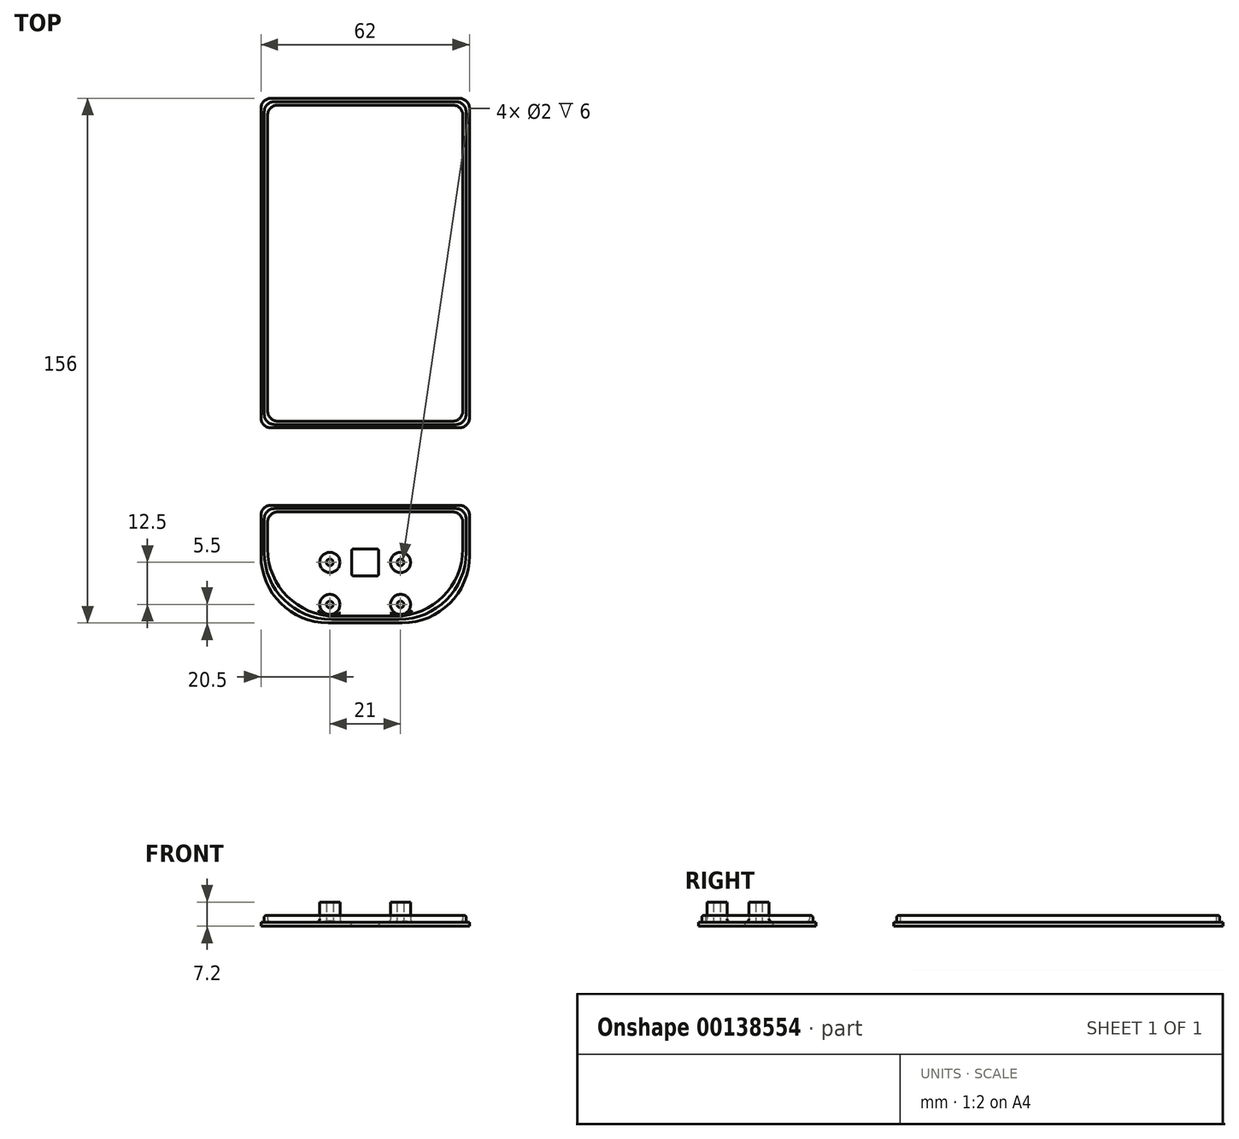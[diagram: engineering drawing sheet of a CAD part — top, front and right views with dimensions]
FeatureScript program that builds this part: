
annotation { "Feature Type Name" : "Feature", "Feature Type Description" : "" }
export const myFeature = defineFeature(function(context is Context, id is Id, definition is map)
    precondition{}
    {
        {
            var Q0;
            Q0=qCreatedBy(makeId("Top.planeOp"),FACE);
            var sketch = newSketch(context, id + "F0", { "sketchPlane" : qUnion([Q0])});
            skLineSegment(sketch, "E0.bottom", {"start": v(-27, 48) * mm, "end": v(27, 48) * mm});
            skLineSegment(sketch, "E0.top", {"start": v(-27, -48) * mm, "end": v(27, -48) * mm});
            skLineSegment(sketch, "E0.left", {"start": v(-30, 45) * mm, "end": v(-30, -45) * mm});
            skLineSegment(sketch, "E0.right", {"start": v(30, 45) * mm, "end": v(30, -45) * mm});
            skPoint(sketch, "E0.middle", {"position": v(0, 0) * mm});
            skPoint(sketch, "E1.visualSharp", {"position": v(-30, 48) * mm});
            skArc(sketch, "E1.filletArc", {"start": v(-27, 48) * mm, "mid": v(-29.12, 47.12) * mm, "end": v(-30, 45) * mm});
            skPoint(sketch, "E2.visualSharp", {"position": v(30, 48) * mm});
            skArc(sketch, "E2.filletArc", {"start": v(30, 45) * mm, "mid": v(29.12, 47.12) * mm, "end": v(27, 48) * mm});
            skPoint(sketch, "E3.visualSharp", {"position": v(30, -48) * mm});
            skArc(sketch, "E3.filletArc", {"start": v(27, -48) * mm, "mid": v(29.12, -47.12) * mm, "end": v(30, -45) * mm});
            skPoint(sketch, "E4.visualSharp", {"position": v(-30, -48) * mm});
            skArc(sketch, "E4.filletArc", {"start": v(-30, -45) * mm, "mid": v(-29.12, -47.12) * mm, "end": v(-27, -48) * mm});
            skLineSegment(sketch, "E5.bottom", {"start": v(-28, 49) * mm, "end": v(28, 49) * mm});
            skLineSegment(sketch, "E5.top", {"start": v(-28, -49) * mm, "end": v(28, -49) * mm});
            skLineSegment(sketch, "E5.left", {"start": v(-31, 46) * mm, "end": v(-31, -46) * mm});
            skLineSegment(sketch, "E5.right", {"start": v(31, 46) * mm, "end": v(31, -46) * mm});
            skPoint(sketch, "E6.visualSharp", {"position": v(-31, -49) * mm});
            skArc(sketch, "E6.filletArc", {"start": v(-31, -46) * mm, "mid": v(-30.12, -48.12) * mm, "end": v(-28, -49) * mm});
            skPoint(sketch, "E7.visualSharp", {"position": v(31, -49) * mm});
            skArc(sketch, "E7.filletArc", {"start": v(28, -49) * mm, "mid": v(30.12, -48.12) * mm, "end": v(31, -46) * mm});
            skPoint(sketch, "E8.visualSharp", {"position": v(31, 49) * mm});
            skArc(sketch, "E8.filletArc", {"start": v(31, 46) * mm, "mid": v(30.12, 48.12) * mm, "end": v(28, 49) * mm});
            skPoint(sketch, "E9.visualSharp", {"position": v(-31, 49) * mm});
            skArc(sketch, "E9.filletArc", {"start": v(-28, 49) * mm, "mid": v(-30.12, 48.12) * mm, "end": v(-31, 46) * mm});
            skLineSegment(sketch, "E10", {"start": v(0, 0) * mm, "end": v(0, 68.08) * mm, "construction": true});
            skPoint(sketch, "E10.endSnap0", {"position": v(0, 48) * mm});
            skPoint(sketch, "E11", {"position": v(0, 42) * mm});
            skLineSegment(sketch, "E12", {"start": v(0, 0) * mm, "end": v(0, -48) * mm, "construction": true});
            skLineSegment(sketch, "E13.bottom", {"start": v(-28, -72) * mm, "end": v(28, -72) * mm});
            skLineSegment(sketch, "E13.top", {"start": v(-11, -107) * mm, "end": v(11, -107) * mm});
            skLineSegment(sketch, "E13.left", {"start": v(-31, -75) * mm, "end": v(-31, -87) * mm});
            skLineSegment(sketch, "E13.right", {"start": v(31, -75) * mm, "end": v(31, -87) * mm});
            skLineSegment(sketch, "E14", {"start": v(0, 1.02) * mm, "end": v(0, 0) * mm, "construction": true});
            skPoint(sketch, "E14.endSnap0", {"position": v(0, -24) * mm});
            skPoint(sketch, "E15", {"position": v(0, -72) * mm});
            skLineSegment(sketch, "E16", {"start": v(-31, -42.86) * mm, "end": v(-31, -72) * mm, "construction": true});
            skLineSegment(sketch, "E17.bottom", {"start": v(-10, -106) * mm, "end": v(10, -106) * mm});
            skLineSegment(sketch, "E17.top", {"start": v(-27, -73) * mm, "end": v(27, -73) * mm});
            skLineSegment(sketch, "E17.left", {"start": v(-30, -86) * mm, "end": v(-30, -76) * mm});
            skLineSegment(sketch, "E17.right", {"start": v(30, -86) * mm, "end": v(30, -76) * mm});
            skPoint(sketch, "E18.visualSharp", {"position": v(-30, -106) * mm});
            skArc(sketch, "E18.filletArc", {"start": v(-30, -86) * mm, "mid": v(-24.14, -100.14) * mm, "end": v(-10, -106) * mm});
            skPoint(sketch, "E19.visualSharp", {"position": v(-30, -73) * mm});
            skArc(sketch, "E19.filletArc", {"start": v(-27, -73) * mm, "mid": v(-29.12, -73.88) * mm, "end": v(-30, -76) * mm});
            skPoint(sketch, "E20.visualSharp", {"position": v(30, -73) * mm});
            skArc(sketch, "E20.filletArc", {"start": v(30, -76) * mm, "mid": v(29.12, -73.88) * mm, "end": v(27, -73) * mm});
            skPoint(sketch, "E21.visualSharp", {"position": v(30, -106) * mm});
            skArc(sketch, "E21.filletArc", {"start": v(10, -106) * mm, "mid": v(24.14, -100.14) * mm, "end": v(30, -86) * mm});
            skPoint(sketch, "E22.visualSharp", {"position": v(-31, -72) * mm});
            skArc(sketch, "E22.filletArc", {"start": v(-28, -72) * mm, "mid": v(-30.12, -72.88) * mm, "end": v(-31, -75) * mm});
            skPoint(sketch, "E23.visualSharp", {"position": v(31, -72) * mm});
            skArc(sketch, "E23.filletArc", {"start": v(31, -75) * mm, "mid": v(30.12, -72.88) * mm, "end": v(28, -72) * mm});
            skPoint(sketch, "E24.visualSharp", {"position": v(-31, -107) * mm});
            skArc(sketch, "E24.filletArc", {"start": v(-31, -87) * mm, "mid": v(-25.14, -101.14) * mm, "end": v(-11, -107) * mm});
            skPoint(sketch, "E25.visualSharp", {"position": v(31, -107) * mm});
            skArc(sketch, "E25.filletArc", {"start": v(11, -107) * mm, "mid": v(25.14, -101.14) * mm, "end": v(31, -87) * mm});
            skLineSegment(sketch, "E26.bottom", {"start": v(-26, 47) * mm, "end": v(26, 47) * mm});
            skLineSegment(sketch, "E26.top", {"start": v(-26, -47) * mm, "end": v(26, -47) * mm});
            skLineSegment(sketch, "E26.left", {"start": v(-29, 44) * mm, "end": v(-29, -44) * mm});
            skLineSegment(sketch, "E26.right", {"start": v(29, 44) * mm, "end": v(29, -44) * mm});
            skPoint(sketch, "E27.visualSharp", {"position": v(-29, 47) * mm});
            skArc(sketch, "E27.filletArc", {"start": v(-26, 47) * mm, "mid": v(-28.12, 46.12) * mm, "end": v(-29, 44) * mm});
            skPoint(sketch, "E28.visualSharp", {"position": v(29, 47) * mm});
            skArc(sketch, "E28.filletArc", {"start": v(29, 44) * mm, "mid": v(28.12, 46.12) * mm, "end": v(26, 47) * mm});
            skPoint(sketch, "E29.visualSharp", {"position": v(29, -47) * mm});
            skArc(sketch, "E29.filletArc", {"start": v(26, -47) * mm, "mid": v(28.12, -46.12) * mm, "end": v(29, -44) * mm});
            skPoint(sketch, "E30.visualSharp", {"position": v(-29, -47) * mm});
            skArc(sketch, "E30.filletArc", {"start": v(-29, -44) * mm, "mid": v(-28.12, -46.12) * mm, "end": v(-26, -47) * mm});
            skLineSegment(sketch, "E31.bottom", {"start": v(-26, -74) * mm, "end": v(26, -74) * mm});
            skLineSegment(sketch, "E31.top", {"start": v(-9, -105) * mm, "end": v(9, -105) * mm});
            skLineSegment(sketch, "E31.left", {"start": v(-29, -77) * mm, "end": v(-29, -85) * mm});
            skLineSegment(sketch, "E31.right", {"start": v(29, -77) * mm, "end": v(29, -85) * mm});
            skPoint(sketch, "E31.middle", {"position": v(0, -89.5) * mm});
            skPoint(sketch, "E32.visualSharp", {"position": v(-29, -74) * mm});
            skArc(sketch, "E32.filletArc", {"start": v(-26, -74) * mm, "mid": v(-28.12, -74.88) * mm, "end": v(-29, -77) * mm});
            skPoint(sketch, "E33.visualSharp", {"position": v(29, -74) * mm});
            skArc(sketch, "E33.filletArc", {"start": v(29, -77) * mm, "mid": v(28.12, -74.88) * mm, "end": v(26, -74) * mm});
            skPoint(sketch, "E34.visualSharp", {"position": v(-29, -105) * mm});
            skArc(sketch, "E34.filletArc", {"start": v(-29, -85) * mm, "mid": v(-23.14, -99.14) * mm, "end": v(-9, -105) * mm});
            skPoint(sketch, "E35.visualSharp", {"position": v(29, -105) * mm});
            skArc(sketch, "E35.filletArc", {"start": v(9, -105) * mm, "mid": v(23.14, -99.14) * mm, "end": v(29, -85) * mm});
            skLineSegment(sketch, "E36", {"start": v(0, 1.02) * mm, "end": v(0, -119.3) * mm, "construction": true});
            skPoint(sketch, "E36.endSnap0", {"position": v(0, -105) * mm});
            skLineSegment(sketch, "E37.bottom", {"start": v(10.5, -101.5) * mm, "end": v(-10.5, -101.5) * mm});
            skLineSegment(sketch, "E37.top", {"start": v(10.5, -89) * mm, "end": v(-10.5, -89) * mm});
            skLineSegment(sketch, "E37.left", {"start": v(10.5, -101.5) * mm, "end": v(10.5, -89) * mm});
            skLineSegment(sketch, "E37.right", {"start": v(-10.5, -101.5) * mm, "end": v(-10.5, -89) * mm});
            skPoint(sketch, "E37.middle", {"position": v(0, -95.25) * mm});
            skCircle(sketch, "E38", {"center": v(10.5, -101.5) * mm, "radius": 1 * mm});
            skCircle(sketch, "E39", {"center": v(-10.5, -101.5) * mm, "radius": 1 * mm});
            skCircle(sketch, "E40", {"center": v(-10.5, -89) * mm, "radius": 1 * mm});
            skCircle(sketch, "E41", {"center": v(10.5, -89) * mm, "radius": 1 * mm});
            skCircle(sketch, "E42", {"center": v(10.5, -101.5) * mm, "radius": 3 * mm});
            skCircle(sketch, "E43", {"center": v(10.5, -89) * mm, "radius": 3 * mm});
            skCircle(sketch, "E44", {"center": v(-10.5, -101.5) * mm, "radius": 3 * mm});
            skCircle(sketch, "E45", {"center": v(-10.5, -89) * mm, "radius": 3 * mm});
            skLineSegment(sketch, "E46.bottom", {"start": v(4, -93) * mm, "end": v(-4, -93) * mm});
            skLineSegment(sketch, "E46.top", {"start": v(4, -85) * mm, "end": v(-4, -85) * mm});
            skLineSegment(sketch, "E46.left", {"start": v(4, -93) * mm, "end": v(4, -85) * mm});
            skLineSegment(sketch, "E46.right", {"start": v(-4, -93) * mm, "end": v(-4, -85) * mm});
            skSolve(sketch);
        }
        {
            var Q0;
            Q0=makeQuery(id+"F0.imprint","IMPRINT",FACE,{"disambiguationData":[TD([[makeQuery(id+"F0.imprint","IMPRINT",EDGE,{"derivedFrom":sQuery(id+"F0.wireOp",EDGE,"E0.bottom")}),1.0]])]});
            var Q1;
            Q1=makeQuery(id+"F0.imprint","IMPRINT",FACE,{"disambiguationData":[TD([[makeQuery(id+"F0.imprint","IMPRINT",EDGE,{"derivedFrom":sQuery(id+"F0.wireOp",EDGE,"E0.bottom")}),-1.0]])]});
            var Q2;
            Q2=makeQuery(id+"F0.imprint","IMPRINT",FACE,{"disambiguationData":[TD([[makeQuery(id+"F0.imprint","IMPRINT",EDGE,{"derivedFrom":sQuery(id+"F0.wireOp",EDGE,"E17.bottom")}),1.0]])]});
            var Q3;
            Q3=makeQuery(id+"F0.imprint","IMPRINT",FACE,{"disambiguationData":[TD([[makeQuery(id+"F0.imprint","IMPRINT",EDGE,{"derivedFrom":sQuery(id+"F0.wireOp",EDGE,"E13.bottom")}),-1.0]])]});
            var Q4;
            Q4=makeQuery(id+"F0.imprint","IMPRINT",FACE,{"disambiguationData":[TD([[makeQuery(id+"F0.imprint","IMPRINT",EDGE,{"derivedFrom":sQuery(id+"F0.wireOp",EDGE,"E26.bottom")}),-1.0]])]});
            var Q5;
            Q5=makeQuery(id+"F0.imprint","IMPRINT",FACE,{"disambiguationData":[TD([[makeQuery(id+"F0.imprint","IMPRINT",EDGE,{"derivedFrom":sQuery(id+"F0.wireOp",EDGE,"E31.bottom")}),-1.0]])]});
            var Q6;
            {var subQ0=sQuery(id+"F0.wireOp",EDGE,"E42");var subQ13=sQuery(id+"F0.wireOp",EDGE,"E37.bottom");var subQ14=makeQuery(id+"F0.imprint","INTERSECT",VERTEX,{"derivedFrom":[subQ13,subQ0]});Q6=makeQuery(id+"F0.imprint","IMPRINT",FACE,{"disambiguationData":[TD([[makeQuery(id+"F0.imprint","IMPRINT",EDGE,{"disambiguationData":[TD([[subQ14,-1.0]])],"derivedFrom":subQ13}),-1.0]])]});}
            var Q7;
            {var subQ0=sQuery(id+"F0.wireOp",EDGE,"E44");var subQ1=sQuery(id+"F0.wireOp",EDGE,"E37.bottom");var subQ2=makeQuery(id+"F0.imprint","INTERSECT",VERTEX,{"derivedFrom":[subQ1,subQ0]});Q7=makeQuery(id+"F0.imprint","IMPRINT",FACE,{"disambiguationData":[TD([[makeQuery(id+"F0.imprint","IMPRINT",EDGE,{"disambiguationData":[TD([[subQ2,-1.0]])],"derivedFrom":subQ1}),1.0]])]});}
            var Q8;
            {var subQ0=sQuery(id+"F0.wireOp",EDGE,"E44");var subQ1=sQuery(id+"F0.wireOp",EDGE,"E37.bottom");var subQ2=makeQuery(id+"F0.imprint","INTERSECT",VERTEX,{"derivedFrom":[subQ1,subQ0]});Q8=makeQuery(id+"F0.imprint","IMPRINT",FACE,{"disambiguationData":[TD([[makeQuery(id+"F0.imprint","IMPRINT",EDGE,{"disambiguationData":[TD([[subQ2,-1.0]])],"derivedFrom":subQ1}),-1.0]])]});}
            var Q9;
            {var subQ0=sQuery(id+"F0.wireOp",EDGE,"E45");var subQ1=sQuery(id+"F0.wireOp",EDGE,"E37.top");var subQ2=makeQuery(id+"F0.imprint","INTERSECT",VERTEX,{"derivedFrom":[subQ1,subQ0]});Q9=makeQuery(id+"F0.imprint","IMPRINT",FACE,{"disambiguationData":[TD([[makeQuery(id+"F0.imprint","IMPRINT",EDGE,{"disambiguationData":[TD([[subQ2,-1.0]])],"derivedFrom":subQ1}),-1.0]])]});}
            var Q10;
            {var subQ0=sQuery(id+"F0.wireOp",EDGE,"E45");var subQ1=sQuery(id+"F0.wireOp",EDGE,"E37.top");var subQ2=makeQuery(id+"F0.imprint","INTERSECT",VERTEX,{"derivedFrom":[subQ1,subQ0]});Q10=makeQuery(id+"F0.imprint","IMPRINT",FACE,{"disambiguationData":[TD([[makeQuery(id+"F0.imprint","IMPRINT",EDGE,{"disambiguationData":[TD([[subQ2,-1.0]])],"derivedFrom":subQ1}),1.0]])]});}
            var Q11;
            {var subQ0=sQuery(id+"F0.wireOp",EDGE,"E37.right");var subQ1=sQuery(id+"F0.wireOp",EDGE,"E37.top");var subQ2=makeQuery(id+"F0.imprint","INTERSECT",VERTEX,{"derivedFrom":[subQ1,subQ0]});Q11=makeQuery(id+"F0.imprint","IMPRINT",FACE,{"disambiguationData":[TD([[makeQuery(id+"F0.imprint","IMPRINT",EDGE,{"disambiguationData":[TD([[subQ2,1.0]])],"derivedFrom":subQ1}),-1.0]])]});}
            var Q12;
            {var subQ0=sQuery(id+"F0.wireOp",EDGE,"E37.right");var subQ1=sQuery(id+"F0.wireOp",EDGE,"E37.bottom");var subQ2=makeQuery(id+"F0.imprint","INTERSECT",VERTEX,{"derivedFrom":[subQ1,subQ0]});Q12=makeQuery(id+"F0.imprint","IMPRINT",FACE,{"disambiguationData":[TD([[makeQuery(id+"F0.imprint","IMPRINT",EDGE,{"disambiguationData":[TD([[subQ2,1.0]])],"derivedFrom":subQ1}),1.0]])]});}
            var Q13;
            {var subQ0=sQuery(id+"F0.wireOp",EDGE,"E37.right");var subQ1=sQuery(id+"F0.wireOp",EDGE,"E37.bottom");var subQ2=makeQuery(id+"F0.imprint","INTERSECT",VERTEX,{"derivedFrom":[subQ1,subQ0]});Q13=makeQuery(id+"F0.imprint","IMPRINT",FACE,{"disambiguationData":[TD([[makeQuery(id+"F0.imprint","IMPRINT",EDGE,{"disambiguationData":[TD([[subQ2,1.0]])],"derivedFrom":subQ1}),-1.0]])]});}
            var Q14;
            {var subQ0=sQuery(id+"F0.wireOp",EDGE,"E37.right");var subQ1=sQuery(id+"F0.wireOp",EDGE,"E37.top");var subQ2=makeQuery(id+"F0.imprint","INTERSECT",VERTEX,{"derivedFrom":[subQ1,subQ0]});Q14=makeQuery(id+"F0.imprint","IMPRINT",FACE,{"disambiguationData":[TD([[makeQuery(id+"F0.imprint","IMPRINT",EDGE,{"disambiguationData":[TD([[subQ2,1.0]])],"derivedFrom":subQ1}),1.0]])]});}
            var Q15;
            {var subQ0=sQuery(id+"F0.wireOp",EDGE,"E41");var subQ1=sQuery(id+"F0.wireOp",EDGE,"E37.top");var subQ2=makeQuery(id+"F0.imprint","INTERSECT",VERTEX,{"derivedFrom":[subQ1,subQ0]});Q15=makeQuery(id+"F0.imprint","IMPRINT",FACE,{"disambiguationData":[TD([[makeQuery(id+"F0.imprint","IMPRINT",EDGE,{"disambiguationData":[TD([[subQ2,-1.0]])],"derivedFrom":subQ1}),1.0]])]});}
            var Q16;
            {var subQ0=sQuery(id+"F0.wireOp",EDGE,"E41");var subQ1=sQuery(id+"F0.wireOp",EDGE,"E37.top");var subQ2=makeQuery(id+"F0.imprint","INTERSECT",VERTEX,{"derivedFrom":[subQ1,subQ0]});Q16=makeQuery(id+"F0.imprint","IMPRINT",FACE,{"disambiguationData":[TD([[makeQuery(id+"F0.imprint","IMPRINT",EDGE,{"disambiguationData":[TD([[subQ2,-1.0]])],"derivedFrom":subQ1}),-1.0]])]});}
            var Q17;
            {var subQ0=sQuery(id+"F0.wireOp",EDGE,"E37.left");var subQ1=sQuery(id+"F0.wireOp",EDGE,"E37.top");var subQ2=makeQuery(id+"F0.imprint","INTERSECT",VERTEX,{"derivedFrom":[subQ1,subQ0]});Q17=makeQuery(id+"F0.imprint","IMPRINT",FACE,{"disambiguationData":[TD([[makeQuery(id+"F0.imprint","IMPRINT",EDGE,{"disambiguationData":[TD([[subQ2,-1.0]])],"derivedFrom":subQ1}),-1.0]])]});}
            var Q18;
            {var subQ0=sQuery(id+"F0.wireOp",EDGE,"E37.left");var subQ1=sQuery(id+"F0.wireOp",EDGE,"E37.top");var subQ2=makeQuery(id+"F0.imprint","INTERSECT",VERTEX,{"derivedFrom":[subQ1,subQ0]});Q18=makeQuery(id+"F0.imprint","IMPRINT",FACE,{"disambiguationData":[TD([[makeQuery(id+"F0.imprint","IMPRINT",EDGE,{"disambiguationData":[TD([[subQ2,-1.0]])],"derivedFrom":subQ1}),1.0]])]});}
            var Q19;
            {var subQ0=sQuery(id+"F0.wireOp",EDGE,"E38");var subQ1=sQuery(id+"F0.wireOp",EDGE,"E37.bottom");var subQ2=makeQuery(id+"F0.imprint","INTERSECT",VERTEX,{"derivedFrom":[subQ1,subQ0]});Q19=makeQuery(id+"F0.imprint","IMPRINT",FACE,{"disambiguationData":[TD([[makeQuery(id+"F0.imprint","IMPRINT",EDGE,{"disambiguationData":[TD([[subQ2,-1.0]])],"derivedFrom":subQ1}),-1.0]])]});}
            var Q20;
            {var subQ0=sQuery(id+"F0.wireOp",EDGE,"E38");var subQ1=sQuery(id+"F0.wireOp",EDGE,"E37.bottom");var subQ2=makeQuery(id+"F0.imprint","INTERSECT",VERTEX,{"derivedFrom":[subQ1,subQ0]});Q20=makeQuery(id+"F0.imprint","IMPRINT",FACE,{"disambiguationData":[TD([[makeQuery(id+"F0.imprint","IMPRINT",EDGE,{"disambiguationData":[TD([[subQ2,-1.0]])],"derivedFrom":subQ1}),1.0]])]});}
            var Q21;
            {var subQ0=sQuery(id+"F0.wireOp",EDGE,"E37.left");var subQ1=sQuery(id+"F0.wireOp",EDGE,"E37.bottom");var subQ2=makeQuery(id+"F0.imprint","INTERSECT",VERTEX,{"derivedFrom":[subQ1,subQ0]});Q21=makeQuery(id+"F0.imprint","IMPRINT",FACE,{"disambiguationData":[TD([[makeQuery(id+"F0.imprint","IMPRINT",EDGE,{"disambiguationData":[TD([[subQ2,-1.0]])],"derivedFrom":subQ1}),1.0]])]});}
            var Q22;
            {var subQ0=sQuery(id+"F0.wireOp",EDGE,"E37.left");var subQ1=sQuery(id+"F0.wireOp",EDGE,"E37.bottom");var subQ2=makeQuery(id+"F0.imprint","INTERSECT",VERTEX,{"derivedFrom":[subQ1,subQ0]});Q22=makeQuery(id+"F0.imprint","IMPRINT",FACE,{"disambiguationData":[TD([[makeQuery(id+"F0.imprint","IMPRINT",EDGE,{"disambiguationData":[TD([[subQ2,-1.0]])],"derivedFrom":subQ1}),-1.0]])]});}
            extrude(context, id + "F1", {"entities" : qUnion([Q0, Q1, Q2, Q3, Q4, Q5, Q6, Q7, Q8, Q9, Q10, Q11, Q12, Q13, Q14, Q15, Q16, Q17, Q18, Q19, Q20, Q21, Q22]), "oppositeDirection" : true, "depth" : 1.2 * mm});
        }
        {
            var Q0;
            Q0=makeQuery(id+"F0.imprint","IMPRINT",FACE,{"disambiguationData":[TD([[makeQuery(id+"F0.imprint","IMPRINT",EDGE,{"derivedFrom":sQuery(id+"F0.wireOp",EDGE,"E17.bottom")}),1.0]])]});
            var Q1;
            Q1=makeQuery(id+"F0.imprint","IMPRINT",FACE,{"disambiguationData":[TD([[makeQuery(id+"F0.imprint","IMPRINT",EDGE,{"derivedFrom":sQuery(id+"F0.wireOp",EDGE,"E0.bottom")}),-1.0]])]});
            extrude(context, id + "F2", {"entities" : qUnion([Q0, Q1]), "operationType" : NewBodyOperationType.ADD, "depth" : 2 * mm});
        }
        {
            var Q0;
            Q0=makeQuery(id+"F2.opExtrude","CAP_EDGE",EDGE,{"disambiguationData":[OSD([sQuery(id+"F0.wireOp",EDGE,"E0.left")])],"isStart":false});
            var Q1;
            Q1=makeQuery(id+"F2.opExtrude","CAP_EDGE",EDGE,{"disambiguationData":[OSD([sQuery(id+"F0.wireOp",EDGE,"E0.bottom")])],"isStart":false});
            var Q2;
            Q2=makeQuery(id+"F2.opExtrude","CAP_EDGE",EDGE,{"disambiguationData":[OSD([sQuery(id+"F0.wireOp",EDGE,"E1.filletArc")])],"isStart":false});
            var Q3;
            Q3=makeQuery(id+"F2.opExtrude","CAP_EDGE",EDGE,{"disambiguationData":[OSD([sQuery(id+"F0.wireOp",EDGE,"E2.filletArc")])],"isStart":false});
            var Q4;
            Q4=makeQuery(id+"F2.opExtrude","CAP_EDGE",EDGE,{"disambiguationData":[OSD([sQuery(id+"F0.wireOp",EDGE,"E0.right")])],"isStart":false});
            var Q5;
            Q5=makeQuery(id+"F2.opExtrude","CAP_EDGE",EDGE,{"disambiguationData":[OSD([sQuery(id+"F0.wireOp",EDGE,"E4.filletArc")])],"isStart":false});
            var Q6;
            Q6=makeQuery(id+"F2.opExtrude","CAP_EDGE",EDGE,{"disambiguationData":[OSD([sQuery(id+"F0.wireOp",EDGE,"E0.top")])],"isStart":false});
            var Q7;
            Q7=makeQuery(id+"F2.opExtrude","CAP_EDGE",EDGE,{"disambiguationData":[OSD([sQuery(id+"F0.wireOp",EDGE,"E3.filletArc")])],"isStart":false});
            var Q8;
            Q8=makeQuery(id+"F2.opExtrude","CAP_EDGE",EDGE,{"disambiguationData":[OSD([sQuery(id+"F0.wireOp",EDGE,"E17.top")])],"isStart":false});
            var Q9;
            Q9=makeQuery(id+"F2.opExtrude","CAP_EDGE",EDGE,{"disambiguationData":[OSD([sQuery(id+"F0.wireOp",EDGE,"E18.filletArc")])],"isStart":false});
            var Q10;
            Q10=makeQuery(id+"F2.opExtrude","CAP_EDGE",EDGE,{"disambiguationData":[OSD([sQuery(id+"F0.wireOp",EDGE,"E17.left")])],"isStart":false});
            var Q11;
            Q11=makeQuery(id+"F2.opExtrude","CAP_EDGE",EDGE,{"disambiguationData":[OSD([sQuery(id+"F0.wireOp",EDGE,"E19.filletArc")])],"isStart":false});
            var Q12;
            Q12=makeQuery(id+"F2.opExtrude","CAP_EDGE",EDGE,{"disambiguationData":[OSD([sQuery(id+"F0.wireOp",EDGE,"E17.bottom")])],"isStart":false});
            var Q13;
            Q13=makeQuery(id+"F2.opExtrude","CAP_EDGE",EDGE,{"disambiguationData":[OSD([sQuery(id+"F0.wireOp",EDGE,"E21.filletArc")])],"isStart":false});
            var Q14;
            Q14=makeQuery(id+"F2.opExtrude","CAP_EDGE",EDGE,{"disambiguationData":[OSD([sQuery(id+"F0.wireOp",EDGE,"E17.right")])],"isStart":false});
            var Q15;
            Q15=makeQuery(id+"F2.opExtrude","CAP_EDGE",EDGE,{"disambiguationData":[OSD([sQuery(id+"F0.wireOp",EDGE,"E20.filletArc")])],"isStart":false});
            fillet(context, id + "F3", {"entities" : qUnion([Q0, Q1, Q2, Q3, Q4, Q5, Q6, Q7, Q8, Q9, Q10, Q11, Q12, Q13, Q14, Q15]), "radius" : .5 * mm, "tangentPropagation" : true, "allowEdgeOverflow" : false});
        }
        {
            var Q0;
            {var subQ0=sQuery(id+"F0.wireOp",EDGE,"E45");var subQ1=sQuery(id+"F0.wireOp",EDGE,"E37.top");var subQ2=makeQuery(id+"F0.imprint","INTERSECT",VERTEX,{"derivedFrom":[subQ1,subQ0]});Q0=makeQuery(id+"F0.imprint","IMPRINT",FACE,{"disambiguationData":[TD([[makeQuery(id+"F0.imprint","IMPRINT",EDGE,{"disambiguationData":[TD([[subQ2,-1.0]])],"derivedFrom":subQ1}),1.0]])]});}
            var Q1;
            {var subQ0=sQuery(id+"F0.wireOp",EDGE,"E45");var subQ1=sQuery(id+"F0.wireOp",EDGE,"E37.top");var subQ2=makeQuery(id+"F0.imprint","INTERSECT",VERTEX,{"derivedFrom":[subQ1,subQ0]});Q1=makeQuery(id+"F0.imprint","IMPRINT",FACE,{"disambiguationData":[TD([[makeQuery(id+"F0.imprint","IMPRINT",EDGE,{"disambiguationData":[TD([[subQ2,-1.0]])],"derivedFrom":subQ1}),-1.0]])]});}
            var Q2;
            {var subQ0=sQuery(id+"F0.wireOp",EDGE,"E41");var subQ1=sQuery(id+"F0.wireOp",EDGE,"E37.top");var subQ2=makeQuery(id+"F0.imprint","INTERSECT",VERTEX,{"derivedFrom":[subQ1,subQ0]});Q2=makeQuery(id+"F0.imprint","IMPRINT",FACE,{"disambiguationData":[TD([[makeQuery(id+"F0.imprint","IMPRINT",EDGE,{"disambiguationData":[TD([[subQ2,-1.0]])],"derivedFrom":subQ1}),1.0]])]});}
            var Q3;
            {var subQ0=sQuery(id+"F0.wireOp",EDGE,"E41");var subQ1=sQuery(id+"F0.wireOp",EDGE,"E37.top");var subQ2=makeQuery(id+"F0.imprint","INTERSECT",VERTEX,{"derivedFrom":[subQ1,subQ0]});Q3=makeQuery(id+"F0.imprint","IMPRINT",FACE,{"disambiguationData":[TD([[makeQuery(id+"F0.imprint","IMPRINT",EDGE,{"disambiguationData":[TD([[subQ2,-1.0]])],"derivedFrom":subQ1}),-1.0]])]});}
            var Q4;
            {var subQ0=sQuery(id+"F0.wireOp",EDGE,"E38");var subQ1=sQuery(id+"F0.wireOp",EDGE,"E37.bottom");var subQ2=makeQuery(id+"F0.imprint","INTERSECT",VERTEX,{"derivedFrom":[subQ1,subQ0]});Q4=makeQuery(id+"F0.imprint","IMPRINT",FACE,{"disambiguationData":[TD([[makeQuery(id+"F0.imprint","IMPRINT",EDGE,{"disambiguationData":[TD([[subQ2,-1.0]])],"derivedFrom":subQ1}),1.0]])]});}
            var Q5;
            {var subQ0=sQuery(id+"F0.wireOp",EDGE,"E38");var subQ1=sQuery(id+"F0.wireOp",EDGE,"E37.bottom");var subQ2=makeQuery(id+"F0.imprint","INTERSECT",VERTEX,{"derivedFrom":[subQ1,subQ0]});Q5=makeQuery(id+"F0.imprint","IMPRINT",FACE,{"disambiguationData":[TD([[makeQuery(id+"F0.imprint","IMPRINT",EDGE,{"disambiguationData":[TD([[subQ2,-1.0]])],"derivedFrom":subQ1}),-1.0]])]});}
            var Q6;
            {var subQ0=sQuery(id+"F0.wireOp",EDGE,"E44");var subQ1=sQuery(id+"F0.wireOp",EDGE,"E37.bottom");var subQ2=makeQuery(id+"F0.imprint","INTERSECT",VERTEX,{"derivedFrom":[subQ1,subQ0]});Q6=makeQuery(id+"F0.imprint","IMPRINT",FACE,{"disambiguationData":[TD([[makeQuery(id+"F0.imprint","IMPRINT",EDGE,{"disambiguationData":[TD([[subQ2,-1.0]])],"derivedFrom":subQ1}),1.0]])]});}
            var Q7;
            {var subQ0=sQuery(id+"F0.wireOp",EDGE,"E44");var subQ1=sQuery(id+"F0.wireOp",EDGE,"E37.bottom");var subQ2=makeQuery(id+"F0.imprint","INTERSECT",VERTEX,{"derivedFrom":[subQ1,subQ0]});Q7=makeQuery(id+"F0.imprint","IMPRINT",FACE,{"disambiguationData":[TD([[makeQuery(id+"F0.imprint","IMPRINT",EDGE,{"disambiguationData":[TD([[subQ2,-1.0]])],"derivedFrom":subQ1}),-1.0]])]});}
            extrude(context, id + "F4", {"entities" : qUnion([Q0, Q1, Q2, Q3, Q4, Q5, Q6, Q7]), "operationType" : NewBodyOperationType.ADD, "depth" : 6 * mm});
        }
        {
            var Q0;
            Q0=makeQuery(id+"F1.opExtrude","SWEPT_EDGE",EDGE,{"disambiguationData":[OSD([sQuery(id+"F0.wireOp",EDGE,"E46.bottom"),sQuery(id+"F0.wireOp",EDGE,"E46.left")])]});
            var Q1;
            Q1=makeQuery(id+"F1.opExtrude","SWEPT_EDGE",EDGE,{"disambiguationData":[OSD([sQuery(id+"F0.wireOp",EDGE,"E46.bottom"),sQuery(id+"F0.wireOp",EDGE,"E46.right")])]});
            var Q2;
            Q2=makeQuery(id+"F1.opExtrude","SWEPT_EDGE",EDGE,{"disambiguationData":[OSD([sQuery(id+"F0.wireOp",EDGE,"E46.top"),sQuery(id+"F0.wireOp",EDGE,"E46.left")])]});
            var Q3;
            Q3=makeQuery(id+"F1.opExtrude","SWEPT_EDGE",EDGE,{"disambiguationData":[OSD([sQuery(id+"F0.wireOp",EDGE,"E46.top"),sQuery(id+"F0.wireOp",EDGE,"E46.right")])]});
            fillet(context, id + "F5", {"entities" : qUnion([Q0, Q1, Q2, Q3]), "radius" : .5 * mm, "tangentPropagation" : true, "allowEdgeOverflow" : false});
        }
        {
            var Q0;
            {var subQ3=sQuery(id+"F0.wireOp",EDGE,"E46.right");var subQ6=sQuery(id+"F0.wireOp",EDGE,"E46.bottom");var subQ7=makeQuery(id+"F1.opExtrude","SWEPT_FACE",FACE,{"disambiguationData":[OSD([subQ6])]});var subQ10=sQuery(id+"F0.wireOp",EDGE,"E46.top");var subQ12=sQuery(id+"F0.wireOp",EDGE,"E46.left");Q0=makeQuery(id+"F4.boolean.opBoolean","SPLIT",FACE,{"disambiguationData":[TD([subQ7])],"derivedFrom":makeQuery(id+"F2.boolean.opBoolean","SPLIT",FACE,{"disambiguationData":[TD([subQ7])],"derivedFrom":makeQuery(id+"F1.opExtrude","CAP_FACE",FACE,{"disambiguationData":[OSD([sQuery(id+"F0.wireOp",EDGE,"E13.bottom"),sQuery(id+"F0.wireOp",EDGE,"E13.top"),sQuery(id+"F0.wireOp",EDGE,"E13.left"),sQuery(id+"F0.wireOp",EDGE,"E13.right"),sQuery(id+"F0.wireOp",EDGE,"E22.filletArc"),sQuery(id+"F0.wireOp",EDGE,"E23.filletArc"),sQuery(id+"F0.wireOp",EDGE,"E24.filletArc"),sQuery(id+"F0.wireOp",EDGE,"E25.filletArc"),subQ6,subQ10,subQ12,subQ3])],"isStart":true})})});}
            fillet(context, id + "F6", {"entities" : qUnion([Q0]), "radius" : 1 * mm, "tangentPropagation" : true, "allowEdgeOverflow" : false});
        }
    });
